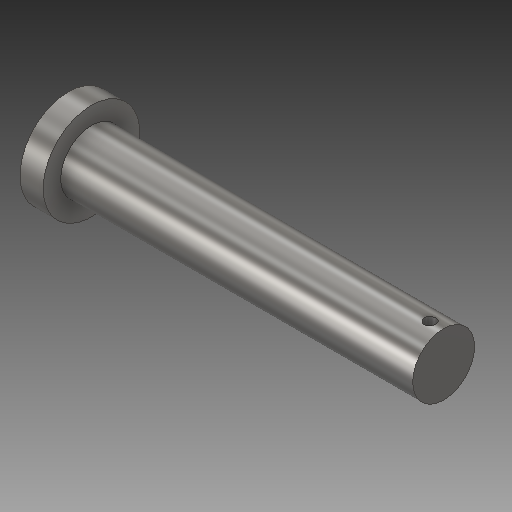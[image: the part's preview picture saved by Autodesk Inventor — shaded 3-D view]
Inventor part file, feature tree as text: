
AUTODESK INVENTOR PART (.ipt)
format: ipt  version: 2018 (Build 220112000, 112)  size: 135,168 bytes
history: native  units: mm
features: extrude x3, sketch x3, plane x1
ambient origin geometry x8: Origin, YZ Plane, XZ Plane, XY Plane, X Axis, Y Axis, Z Axis, Center Point
bodies: Solid1 (feature_tree)
feature tree (7):
  extrude  "Extrusion1"  Depth=12.0mm TaperAngle=0.0deg
  extrude  "Extrusion2"  Depth=182.0mm TaperAngle=0.0deg
  plane  "Work Plane1"
  extrude  "Extrusion3"  Depth=16.0mm
  sketch  "Sketch1"  dims[d0=50.0mm d1=12.0mm d2=0.0mm]
  sketch  "Sketch2"  dims[d3=32.0mm d4=182.0mm d5=0.0mm]
  sketch  "Sketch3"  dims[d6=16.0mm d7=6.0mm d8=170.0mm d9=0.0mm]
